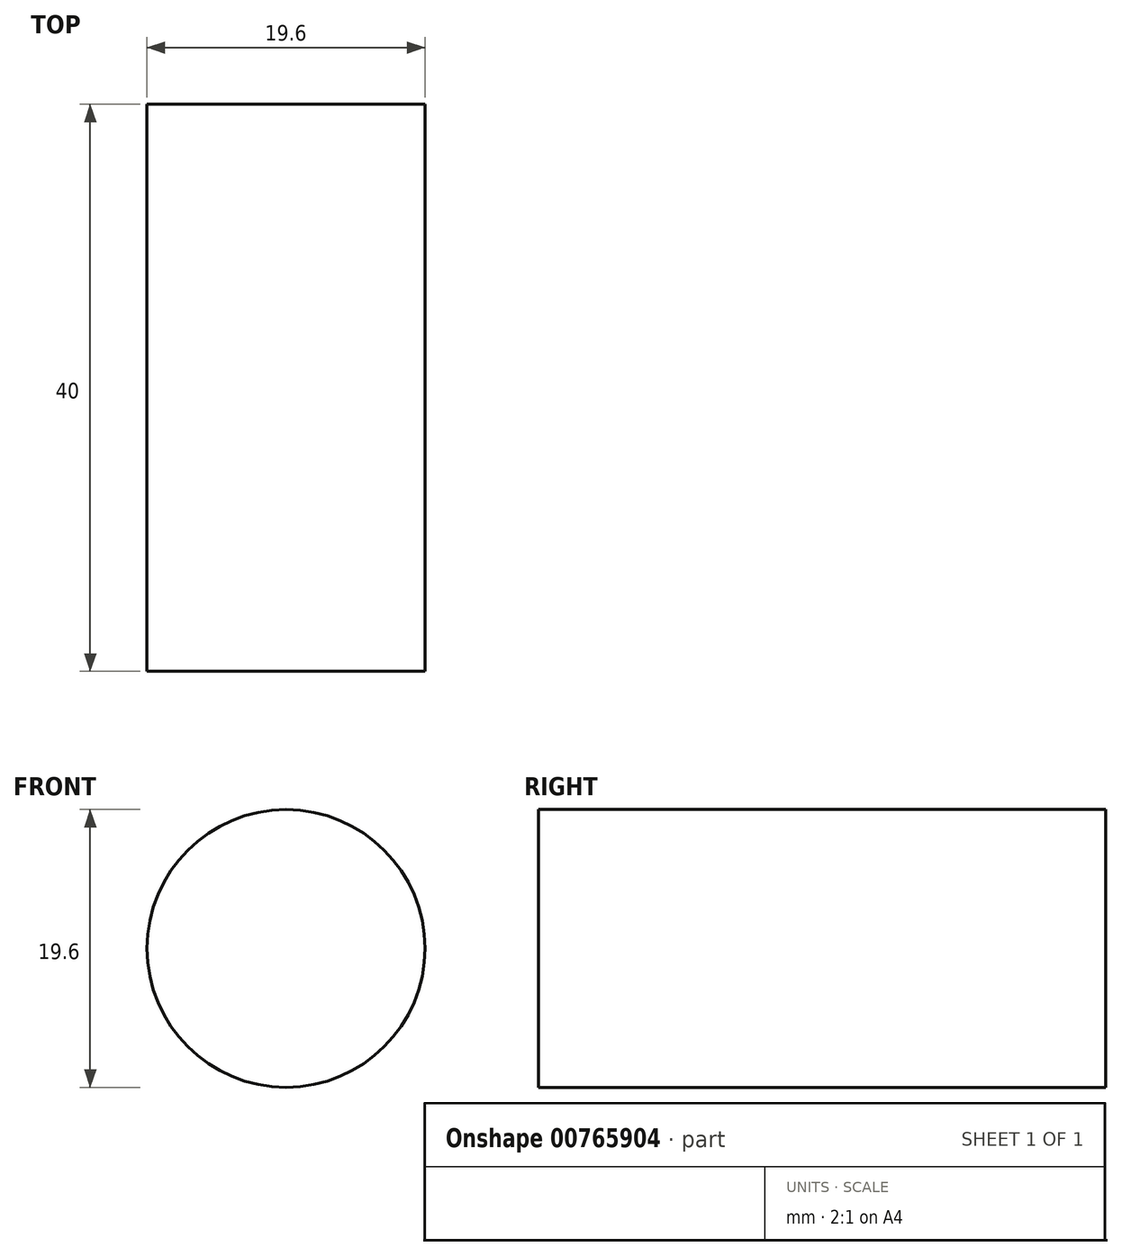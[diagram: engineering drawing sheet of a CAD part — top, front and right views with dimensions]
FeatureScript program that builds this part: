
annotation { "Feature Type Name" : "Feature", "Feature Type Description" : "" }
export const myFeature = defineFeature(function(context is Context, id is Id, definition is map)
    precondition{}
    {
        {
            var Q0;
            Q0=qCreatedBy(makeId("Front.planeOp"),FACE);
            var sketch = newSketch(context, id + "F0", { "sketchPlane" : qUnion([Q0])});
            skCircle(sketch, "E0", {"center": v(0, 0) * mm, "radius": 9.8 * mm});
            skSolve(sketch);
        }
        {
            var Q0;
            Q0=makeQuery(id+"F0.imprint","IMPRINT",FACE,{"disambiguationData":[TD([[makeQuery(id+"F0.imprint","IMPRINT",EDGE,{"derivedFrom":sQuery(id+"F0.wireOp",EDGE,"E0")}),1.0]])]});
            extrude(context, id + "F1", {"entities" : qUnion([Q0]), "oppositeDirection" : true, "depth" : 40 * mm, "offsetDistance" : 25 * mm});
        }
    });
